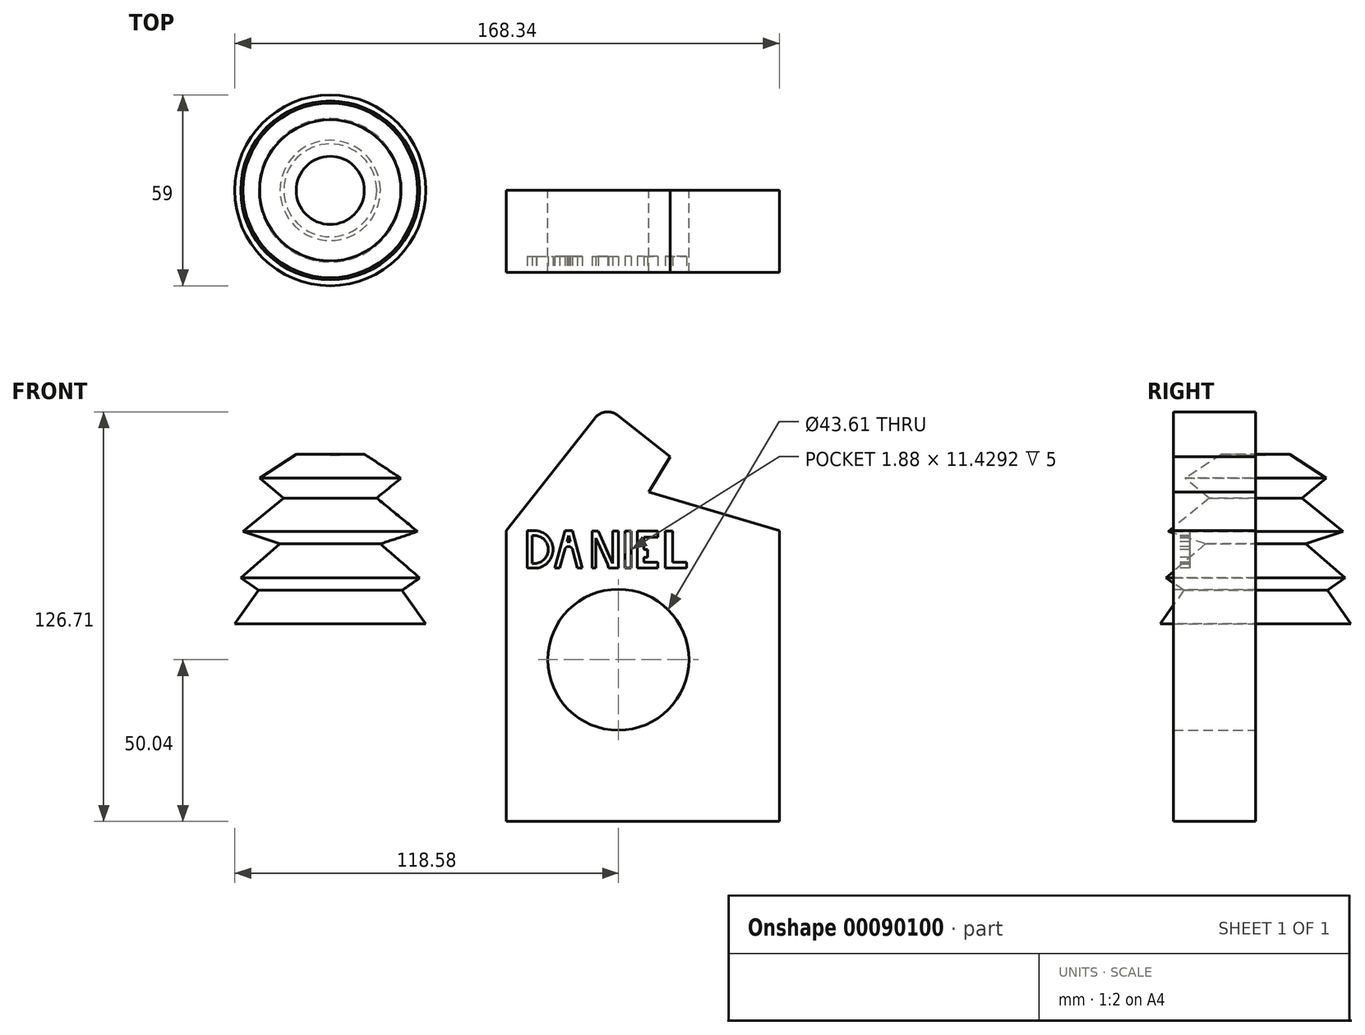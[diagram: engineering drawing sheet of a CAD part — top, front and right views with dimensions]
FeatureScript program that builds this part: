
annotation { "Feature Type Name" : "Feature", "Feature Type Description" : "" }
export const myFeature = defineFeature(function(context is Context, id is Id, definition is map)
    precondition{}
    {
        {
            var Q0;
            Q0=qCreatedBy(makeId("Front.planeOp"),FACE);
            var sketch = newSketch(context, id + "F0", { "sketchPlane" : qUnion([Q0])});
            skLineSegment(sketch, "E0.top", {"start": v(-34.68, -50.04) * mm, "end": v(49.76, -50.04) * mm});
            skLineSegment(sketch, "E0.left", {"start": v(-34.68, 39.86) * mm, "end": v(-34.68, -50.04) * mm});
            skLineSegment(sketch, "E0.right", {"start": v(49.76, 39.86) * mm, "end": v(49.76, -50.04) * mm});
            skCircle(sketch, "E1", {"center": v(0, 0) * mm, "radius": 21.8 * mm});
            skLineSegment(sketch, "E2", {"start": v(-34.68, 39.86) * mm, "end": v(-7.24, 74.76) * mm});
            skLineSegment(sketch, "E3", {"start": v(-0.22, 75.6) * mm, "end": v(16, 62.84) * mm});
            skLineSegment(sketch, "E4", {"start": v(16, 62.84) * mm, "end": v(9.42, 51.93) * mm});
            skLineSegment(sketch, "E5", {"start": v(9.42, 51.93) * mm, "end": v(49.76, 39.86) * mm});
            skPoint(sketch, "E6.visualSharp", {"position": v(-4.15, 78.7) * mm});
            skArc(sketch, "E6.filletArc", {"start": v(-0.22, 75.6) * mm, "mid": v(-3.9, 76.63) * mm, "end": v(-7.24, 74.76) * mm});
            skSolve(sketch);
        }
        {
            var Q0;
            Q0=makeQuery(id+"F0.imprint","IMPRINT",FACE,{"disambiguationData":[TD([[makeQuery(id+"F0.imprint","IMPRINT",EDGE,{"derivedFrom":sQuery(id+"F0.wireOp",EDGE,"E0.top")}),1.0]])]});
            extrude(context, id + "F1", {"entities" : qUnion([Q0]), "depth" : 25.4 * mm});
        }
        {
            var Q0;
            Q0=qCreatedBy(makeId("Front.planeOp"),FACE);
            var sketch = newSketch(context, id + "F2", { "sketchPlane" : qUnion([Q0])});
            skLineSegment(sketch, "E7", {"start": v(-89.08, 63.22) * mm, "end": v(-89.08, 11.11) * mm});
            skLineSegment(sketch, "E8", {"start": v(-89.08, 11.11) * mm, "end": v(-59.58, 11.11) * mm});
            skLineSegment(sketch, "E9", {"start": v(-59.58, 11.11) * mm, "end": v(-66.85, 21.45) * mm});
            skLineSegment(sketch, "E10", {"start": v(-66.85, 21.45) * mm, "end": v(-61.41, 25.28) * mm});
            skLineSegment(sketch, "E11", {"start": v(-61.41, 25.28) * mm, "end": v(-73.56, 35.82) * mm});
            skLineSegment(sketch, "E12", {"start": v(-73.56, 35.82) * mm, "end": v(-62.07, 39.65) * mm});
            skLineSegment(sketch, "E13", {"start": v(-62.07, 39.65) * mm, "end": v(-74.7, 50) * mm});
            skLineSegment(sketch, "E14", {"start": v(-74.7, 50) * mm, "end": v(-67.24, 56.13) * mm});
            skLineSegment(sketch, "E15", {"start": v(-67.24, 56.13) * mm, "end": v(-78.54, 63.6) * mm});
            skLineSegment(sketch, "E16", {"start": v(-78.54, 63.6) * mm, "end": v(-89.08, 63.22) * mm});
            skSolve(sketch);
        }
        {
            var Q0;
            Q0=makeQuery(id+"F2.imprint","IMPRINT",FACE,{"disambiguationData":[TD([[makeQuery(id+"F2.imprint","IMPRINT",EDGE,{"derivedFrom":sQuery(id+"F2.wireOp",EDGE,"E7")}),1.0]])]});
            var Q1;
            Q1=sQuery(id+"F2.wireOp",EDGE,"E7");
            revolve(context, id + "F3", {"entities" : qUnion([Q0]), "axis" : qUnion([Q1]), "revolveType" : RevolveType.FULL});
        }
        {
            var Q0;
            Q0=makeQuery(id+"F1.opExtrude","CAP_FACE",FACE,{"disambiguationData":[OSD([sQuery(id+"F0.wireOp",EDGE,"E0.top"),sQuery(id+"F0.wireOp",EDGE,"E0.left"),sQuery(id+"F0.wireOp",EDGE,"E0.right"),sQuery(id+"F0.wireOp",EDGE,"E1"),sQuery(id+"F0.wireOp",EDGE,"E2"),sQuery(id+"F0.wireOp",EDGE,"E3"),sQuery(id+"F0.wireOp",EDGE,"E4"),sQuery(id+"F0.wireOp",EDGE,"E5"),sQuery(id+"F0.wireOp",EDGE,"E6.filletArc")])],"isStart":false});
            var sketch = newSketch(context, id + "F4", { "sketchPlane" : qUnion([Q0])});
            skLineSegment(sketch, "E17", {"start": v(-28.13, 39.86) * mm, "end": v(-28.13, 28.32) * mm});
            skLineSegment(sketch, "E18", {"start": v(-28.13, 28.32) * mm, "end": v(-25.31, 28.32) * mm});
            skLineSegment(sketch, "E19", {"start": v(-28.13, 39.86) * mm, "end": v(-25.31, 39.86) * mm});
            skArc(sketch, "E20", {"start": v(-25.31, 28.32) * mm, "mid": v(-20.17, 34.1) * mm, "end": v(-25.31, 39.86) * mm});
            skArc(sketch, "E21.0", {"start": v(-25.4, 29.82) * mm, "mid": v(-21.67, 34.1) * mm, "end": v(-25.4, 38.36) * mm});
            skLineSegment(sketch, "E21.1", {"start": v(-26.63, 29.82) * mm, "end": v(-25.4, 29.82) * mm});
            skLineSegment(sketch, "E21.2", {"start": v(-26.63, 38.36) * mm, "end": v(-26.63, 29.82) * mm});
            skLineSegment(sketch, "E21.3", {"start": v(-26.63, 38.36) * mm, "end": v(-25.4, 38.36) * mm});
            skLineSegment(sketch, "E22", {"start": v(-16.53, 39.86) * mm, "end": v(-19.67, 28.32) * mm});
            skPoint(sketch, "E22.endSnap0", {"position": v(-26.72, 28.32) * mm});
            skLineSegment(sketch, "E23", {"start": v(-19.67, 28.32) * mm, "end": v(-18.11, 28.32) * mm});
            skLineSegment(sketch, "E24", {"start": v(-18.11, 28.32) * mm, "end": v(-16.51, 34.22) * mm});
            skLineSegment(sketch, "E25", {"start": v(-15.55, 34.96) * mm, "end": v(-15.39, 34.96) * mm});
            skPoint(sketch, "E26.endSnap0", {"position": v(-18.89, 28.32) * mm});
            skPoint(sketch, "E27.endSnap0", {"position": v(-14.24, 31.4) * mm});
            skLineSegment(sketch, "E28", {"start": v(-14.24, 39.86) * mm, "end": v(-16.53, 39.86) * mm});
            skLineSegment(sketch, "E29", {"start": v(-15.89, 36.52) * mm, "end": v(-15.39, 36.52) * mm});
            skLineSegment(sketch, "E30", {"start": v(-15.39, 38.36) * mm, "end": v(-15.89, 36.52) * mm});
            skLineSegment(sketch, "E31", {"start": v(-15.39, 38.36) * mm, "end": v(-15.39, 27.34) * mm});
            skLineSegment(sketch, "E32.MirrorCS", {"start": v(-14.89, 36.52) * mm, "end": v(-15.39, 36.52) * mm});
            skLineSegment(sketch, "E33.MirrorCS", {"start": v(-15.39, 38.36) * mm, "end": v(-14.89, 36.52) * mm});
            skLineSegment(sketch, "E34.MirrorCS", {"start": v(-14.24, 39.86) * mm, "end": v(-11.1, 28.32) * mm});
            skLineSegment(sketch, "E35.MirrorCS", {"start": v(-15.23, 34.96) * mm, "end": v(-15.39, 34.96) * mm});
            skLineSegment(sketch, "E36.MirrorCS", {"start": v(-12.66, 28.32) * mm, "end": v(-14.26, 34.22) * mm});
            skLineSegment(sketch, "E37.MirrorCS", {"start": v(-11.1, 28.32) * mm, "end": v(-12.66, 28.32) * mm});
            skLineSegment(sketch, "E38", {"start": v(-8.15, 28.32) * mm, "end": v(-8.15, 39.75) * mm});
            skLineSegment(sketch, "E39", {"start": v(-8.15, 39.75) * mm, "end": v(-6.17, 39.75) * mm});
            skLineSegment(sketch, "E40", {"start": v(-6.17, 39.75) * mm, "end": v(-1.79, 29.8) * mm});
            skLineSegment(sketch, "E41", {"start": v(-1.79, 29.8) * mm, "end": v(-1.79, 39.75) * mm});
            skLineSegment(sketch, "E42", {"start": v(-1.79, 39.75) * mm, "end": v(0, 39.75) * mm});
            skLineSegment(sketch, "E43", {"start": v(0, 39.75) * mm, "end": v(0, 28.32) * mm});
            skLineSegment(sketch, "E44", {"start": v(-3.35, 29.57) * mm, "end": v(-6.91, 37.67) * mm});
            skLineSegment(sketch, "E45", {"start": v(-6.91, 37.67) * mm, "end": v(-6.91, 28.32) * mm});
            skLineSegment(sketch, "E46", {"start": v(-3.35, 29.57) * mm, "end": v(-3.01, 28.32) * mm});
            skLineSegment(sketch, "E47", {"start": v(2.03, 39.75) * mm, "end": v(2.03, 28.32) * mm});
            skLineSegment(sketch, "E48", {"start": v(2.03, 28.32) * mm, "end": v(3.91, 28.32) * mm});
            skLineSegment(sketch, "E49", {"start": v(3.91, 28.32) * mm, "end": v(3.91, 39.75) * mm});
            skLineSegment(sketch, "E50", {"start": v(3.91, 39.75) * mm, "end": v(2.03, 39.75) * mm});
            skLineSegment(sketch, "E51", {"start": v(5.88, 39.75) * mm, "end": v(5.88, 28.32) * mm});
            skLineSegment(sketch, "E52", {"start": v(5.88, 28.32) * mm, "end": v(12.23, 28.32) * mm});
            skLineSegment(sketch, "E53", {"start": v(12.23, 28.32) * mm, "end": v(12.23, 30.16) * mm});
            skLineSegment(sketch, "E54", {"start": v(12.23, 30.16) * mm, "end": v(7.84, 30.16) * mm});
            skLineSegment(sketch, "E55", {"start": v(7.84, 30.16) * mm, "end": v(7.84, 31.33) * mm});
            skLineSegment(sketch, "E56", {"start": v(8.14, 31.63) * mm, "end": v(9.06, 31.63) * mm});
            skLineSegment(sketch, "E57", {"start": v(9.06, 31.63) * mm, "end": v(9.06, 34.09) * mm});
            skLineSegment(sketch, "E58", {"start": v(9.06, 34.09) * mm, "end": v(8.14, 34.09) * mm});
            skLineSegment(sketch, "E59", {"start": v(7.84, 34.39) * mm, "end": v(7.84, 37.89) * mm});
            skLineSegment(sketch, "E60", {"start": v(7.84, 37.89) * mm, "end": v(12.23, 37.89) * mm});
            skLineSegment(sketch, "E61", {"start": v(12.23, 37.89) * mm, "end": v(12.23, 39.75) * mm});
            skLineSegment(sketch, "E62", {"start": v(12.23, 39.75) * mm, "end": v(5.88, 39.75) * mm});
            skLineSegment(sketch, "E63", {"start": v(14.53, 39.75) * mm, "end": v(14.53, 28.32) * mm});
            skLineSegment(sketch, "E64", {"start": v(14.53, 28.32) * mm, "end": v(21.08, 28.32) * mm});
            skLineSegment(sketch, "E65", {"start": v(21.08, 28.32) * mm, "end": v(21.08, 30.16) * mm});
            skLineSegment(sketch, "E66", {"start": v(21.08, 30.16) * mm, "end": v(16.78, 30.16) * mm});
            skLineSegment(sketch, "E67", {"start": v(16.78, 30.16) * mm, "end": v(16.78, 39.75) * mm});
            skLineSegment(sketch, "E68", {"start": v(16.78, 39.75) * mm, "end": v(14.53, 39.75) * mm});
            skLineSegment(sketch, "E69", {"start": v(-8.15, 28.32) * mm, "end": v(-6.91, 28.32) * mm});
            skLineSegment(sketch, "E70", {"start": v(-3.01, 28.32) * mm, "end": v(0, 28.32) * mm});
            skPoint(sketch, "E71.visualSharp", {"position": v(-14.46, 34.96) * mm});
            skArc(sketch, "E71.filletArc", {"start": v(-14.26, 34.22) * mm, "mid": v(-14.62, 34.75) * mm, "end": v(-15.23, 34.96) * mm});
            skPoint(sketch, "E72.visualSharp", {"position": v(-16.31, 34.96) * mm});
            skArc(sketch, "E72.filletArc", {"start": v(-15.55, 34.96) * mm, "mid": v(-16.15, 34.75) * mm, "end": v(-16.51, 34.22) * mm});
            skPoint(sketch, "E73.visualSharp", {"position": v(7.84, 31.63) * mm});
            skArc(sketch, "E73.filletArc", {"start": v(8.14, 31.63) * mm, "mid": v(7.93, 31.54) * mm, "end": v(7.84, 31.33) * mm});
            skPoint(sketch, "E74.visualSharp", {"position": v(7.84, 34.09) * mm});
            skArc(sketch, "E74.filletArc", {"start": v(7.84, 34.39) * mm, "mid": v(7.93, 34.17) * mm, "end": v(8.14, 34.09) * mm});
            skSolve(sketch);
        }
        {
            var Q0;
            Q0=makeQuery(id+"F4.imprint","IMPRINT",FACE,{"disambiguationData":[TD([[makeQuery(id+"F4.imprint","IMPRINT",EDGE,{"derivedFrom":sQuery(id+"F4.wireOp",EDGE,"E17")}),1.0]])]});
            var Q1;
            Q1=makeQuery(id+"F4.imprint","IMPRINT",FACE,{"disambiguationData":[TD([[makeQuery(id+"F4.imprint","IMPRINT",EDGE,{"derivedFrom":sQuery(id+"F4.wireOp",EDGE,"E22")}),1.0]])]});
            var Q2;
            Q2=makeQuery(id+"F4.imprint","IMPRINT",FACE,{"disambiguationData":[TD([[makeQuery(id+"F4.imprint","IMPRINT",EDGE,{"derivedFrom":sQuery(id+"F4.wireOp",EDGE,"E47")}),1.0]])]});
            var Q3;
            Q3=makeQuery(id+"F4.imprint","IMPRINT",FACE,{"disambiguationData":[TD([[makeQuery(id+"F4.imprint","IMPRINT",EDGE,{"derivedFrom":sQuery(id+"F4.wireOp",EDGE,"E51")}),1.0]])]});
            var Q4;
            Q4=makeQuery(id+"F4.imprint","IMPRINT",FACE,{"disambiguationData":[TD([[makeQuery(id+"F4.imprint","IMPRINT",EDGE,{"derivedFrom":sQuery(id+"F4.wireOp",EDGE,"E63")}),1.0]])]});
            var Q5;
            Q5=makeQuery(id+"F4.imprint","IMPRINT",FACE,{"disambiguationData":[TD([[makeQuery(id+"F4.imprint","IMPRINT",EDGE,{"derivedFrom":sQuery(id+"F4.wireOp",EDGE,"E38")}),-1.0]])]});
            extrude(context, id + "F5", {"entities" : qUnion([Q0, Q1, Q2, Q3, Q4, Q5]), "operationType" : NewBodyOperationType.REMOVE, "oppositeDirection" : true, "depth" : 5 * mm});
        }
    });
